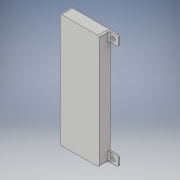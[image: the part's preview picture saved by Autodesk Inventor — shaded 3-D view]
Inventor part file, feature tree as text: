
AUTODESK INVENTOR PART (.ipt)
format: ipt  version: 2018 (Build 220112000, 112)  size: 147,456 bytes
history: native  units: in
note: dims shown in document units (in); Inventor stores cm internally (conversion verified against a paired STEP export)
features: reference x6, other x5, fillet x3, sketch x2, extrude x2, plane x1
ambient origin geometry x8: Origin, YZ Plane, XZ Plane, XY Plane, X Axis, Y Axis, Z Axis, Center Point
bodies: Solid1 (feature_tree)
feature tree (19):
  sketch  "Sketch1"  dims[d0=0.1in d1=0.0in d2=0.25in]
  plane  "Work Plane1"
  extrude  "Extrusion1"  Depth=0.25in
  extrude  "Extrusion2"  Depth=0.0394in
  fillet  "Fillet1"  Radius=0.0394in
  fillet  "Fillet2"  Radius=0.0394in
  fillet  "Fillet3"  Radius=0.0394in
  reference  "Reference1"
  reference  "Reference2"
  reference  "Reference3"
  reference  "Reference4"
  reference  "Reference5"
  reference  "Reference6"
  sketch  "Sketch2"  dims[d3=0.25in d5=0.0984in d6=0.0394in d7=0.0in d8=0.0394in d9=0.0394in d10=0.0394in]
  other  "<userpath>\OneDrive\Documents\Inventor\TSA\2018\Animatronics\Tortoise\AssemblyTURTLE.iam"
  other  "AssemblyTURTLE.iam"
  other  "AssemblyNEWarm:1"
  other  "newShoulder:1"
  other  "Rack:5"
